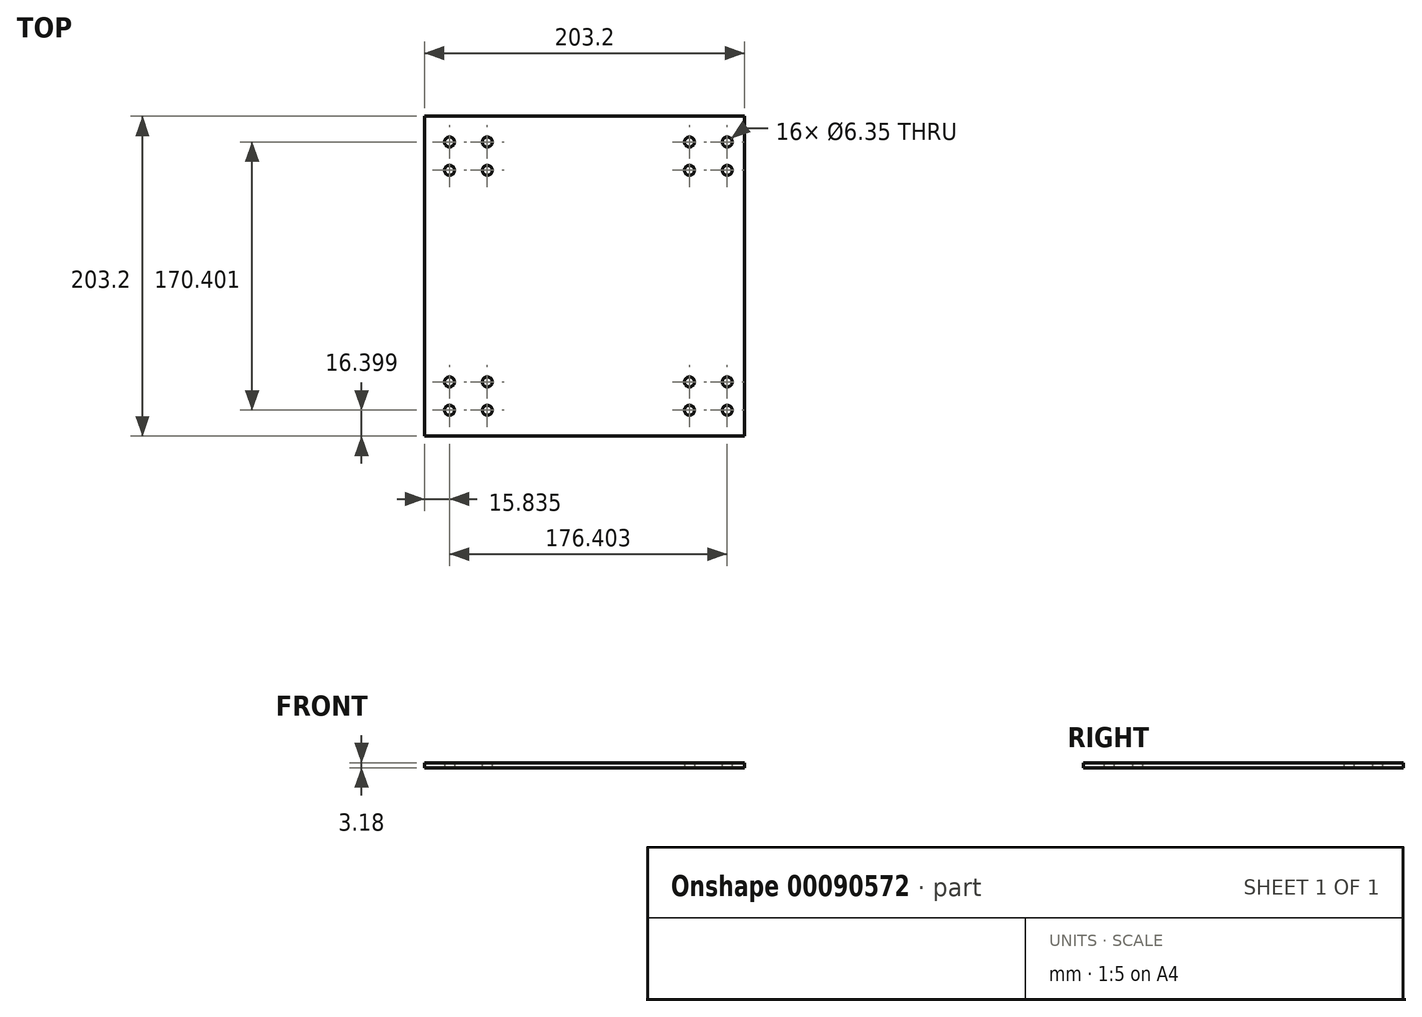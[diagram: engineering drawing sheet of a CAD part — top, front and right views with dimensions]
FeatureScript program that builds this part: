
annotation { "Feature Type Name" : "Feature", "Feature Type Description" : "" }
export const myFeature = defineFeature(function(context is Context, id is Id, definition is map)
    precondition{}
    {
        {
            var Q0;
            Q0=qCreatedBy(makeId("Top.planeOp"),FACE);
            var sketch = newSketch(context, id + "F0", { "sketchPlane" : qUnion([Q0])});
            skPoint(sketch, "E0.middle", {"position": v(0, 0) * mm});
            skPoint(sketch, "E1.middle", {"position": v(-73.76, 76.2) * mm});
            skCircle(sketch, "E2", {"center": v(-85.76, 85.2) * mm, "radius": 3.18 * mm});
            skCircle(sketch, "E3.0.1.0", {"center": v(-85.76, 67.2) * mm, "radius": 3.18 * mm});
            skCircle(sketch, "E3.1.0.0", {"center": v(-61.76, 85.2) * mm, "radius": 3.18 * mm});
            skCircle(sketch, "E3.1.1.0", {"center": v(-61.76, 67.2) * mm, "radius": 3.18 * mm});
            skCircle(sketch, "E4.0.1.0", {"center": v(-85.76, -67.2) * mm, "radius": 3.18 * mm});
            skCircle(sketch, "E4.0.1.1", {"center": v(-61.76, -67.2) * mm, "radius": 3.18 * mm});
            skCircle(sketch, "E4.0.1.2", {"center": v(-61.76, -85.2) * mm, "radius": 3.18 * mm});
            skCircle(sketch, "E4.0.1.3", {"center": v(-85.76, -85.2) * mm, "radius": 3.18 * mm});
            skCircle(sketch, "E4.1.0.0", {"center": v(66.64, 85.2) * mm, "radius": 3.18 * mm});
            skCircle(sketch, "E4.1.0.1", {"center": v(90.64, 85.2) * mm, "radius": 3.18 * mm});
            skCircle(sketch, "E4.1.0.2", {"center": v(90.64, 67.2) * mm, "radius": 3.18 * mm});
            skCircle(sketch, "E4.1.0.3", {"center": v(66.64, 67.2) * mm, "radius": 3.18 * mm});
            skCircle(sketch, "E4.1.1.0", {"center": v(66.64, -67.2) * mm, "radius": 3.18 * mm});
            skCircle(sketch, "E4.1.1.1", {"center": v(90.64, -67.2) * mm, "radius": 3.18 * mm});
            skCircle(sketch, "E4.1.1.2", {"center": v(90.64, -85.2) * mm, "radius": 3.18 * mm});
            skCircle(sketch, "E4.1.1.3", {"center": v(66.64, -85.2) * mm, "radius": 3.18 * mm});
            skSolve(sketch);
        }
        {
            var Q0;
            Q0=qCreatedBy(makeId("Top.planeOp"),FACE);
            var sketch = newSketch(context, id + "F1", { "sketchPlane" : qUnion([Q0])});
            skLineSegment(sketch, "E5.bottom", {"start": v(101.6, 101.6) * mm, "end": v(-101.6, 101.6) * mm});
            skLineSegment(sketch, "E5.top", {"start": v(101.6, -101.6) * mm, "end": v(-101.6, -101.6) * mm});
            skLineSegment(sketch, "E5.left", {"start": v(101.6, 101.6) * mm, "end": v(101.6, -101.6) * mm});
            skLineSegment(sketch, "E5.right", {"start": v(-101.6, 101.6) * mm, "end": v(-101.6, -101.6) * mm});
            skPoint(sketch, "E5.middle", {"position": v(0, 0) * mm});
            skSolve(sketch);
        }
        {
            var Q0;
            Q0 = qSketchRegion(id + "F1", true);
            extrude(context, id + "F2", {"entities" : qUnion([Q0]), "depth" : 3.17 * mm});
        }
        {
            var Q0;
            Q0 = qSketchRegion(id + "F0", true);
            var Q1;
            Q1=makeQuery(id+"F2.opExtrude","CAP_FACE",FACE,{"disambiguationData":[OSD([sQuery(id+"F1.wireOp",EDGE,"E5.bottom"),sQuery(id+"F1.wireOp",EDGE,"E5.top"),sQuery(id+"F1.wireOp",EDGE,"E5.left"),sQuery(id+"F1.wireOp",EDGE,"E5.right")])],"isStart":false});
            extrude(context, id + "F3", {"entities" : qUnion([Q0]), "operationType" : NewBodyOperationType.REMOVE, "endBound" : BoundingType.UP_TO_SURFACE, "endBoundEntityFace" : qUnion([Q1]), "depth" : 3.17 * mm});
        }
    });
